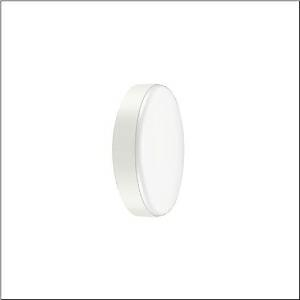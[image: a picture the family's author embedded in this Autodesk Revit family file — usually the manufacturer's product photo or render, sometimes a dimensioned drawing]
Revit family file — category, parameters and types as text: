
# Revit family: rondel_31_51wc10da42a
name_source: partatom
category: Lighting Fixtures
units: mm (PartAtom-declared; Revit-internal decimal feet)

## family parameters
Cut with Voids When Loaded = No
Host = Face
Light Source = No
Part Type = Normal
Room Calculation Point = No
Round Connector Dimension = Use Diameter
Shared = No

## types (1)
- Rondel 31 (1 x LED, 2550 lm, 19 W, 4000K)
    Apparent Load = 19 VA
    CIE Flux Codes = 44 75 94 94 100
    Color Rendering = 80
    Color Temperature = 4000K
    Default Elevation = 1800 mm
    Description = Rondel 31, wall and ceiling luminaire, primary optical cover: cover, of PC, opal, light emission: direct distribution, primary light characteristic: symmetric, installation type: surface-mounted, LED, rated luminous flux: 2.400lm, luminous efficacy: 125lm/W, light colour: 840, colour temperature: 4000K, with terminal, 5-pole, max. 2.5mm², mains connection: 220..240V, AC, 50/60Hz, rated input power: 19W, luminaire housing, of PC, traffic white (RAL 9016), diameter: 350mm, protection rating (complete): IP65, insulation class (complete): insulation class II (safety insulation), certification: CE, impact resistance: IK10, permissible storage temperature: -20..+60°C, packaging unit: 1 piece
    Height = 97 mm
    Lamp = 1 x LED
    Lamp Light Flux = 2550 lm
    Lamp Power = 19 W
    Lamp count = 1
    Length = 350 mm
    Luminous efficacy = 134 lm/W
    Manufacturer = Siteco
    ModVariant = No
    Model = 51WC10DA42A
    Mounting Place = Ceiling
    Mounting Type = Surface mounted
    Number of Poles = 1
    OnlyDefault = Yes
    Power Factor = 1
    Product Name = Rondel 31
    Product group = wall and ceiling luminaire
    ProductGroupID = 301
    Protection Class = Protection class II
    Protection Degree = IP 65
    RLX_Detail_Level = 1
    RlxData = <blob elided: 29485 chars, md5=c6421017>
    Socket = socket
    Standby Power = 0 W
    System Light Flux = 2550 lm
    System Power = 19 W
    Type Comments = Product without accessories
    Type Image = l_1007027.jpg
    URL = http://relux.com
    VarID = ---
    Voltage = 0 V
    Weight = 0.00 kg
    Width = 0 mm  [stored 0 ft]

note: [stored X ft] marks values corroborated as IEEE doubles in the binary element streams (Revit-internal decimal feet)

## geometry (parser evidence)
native form markers: Blend x4, Sweep x11
no freeform markers — native parametric forms only
